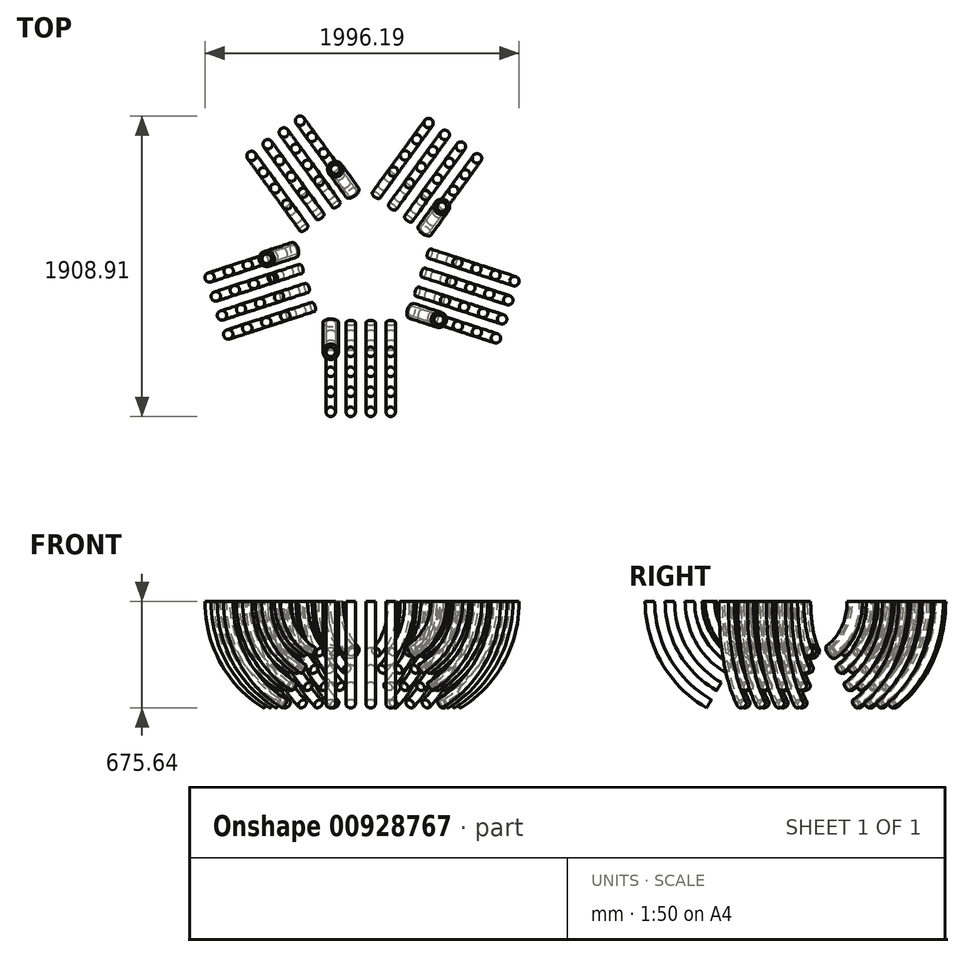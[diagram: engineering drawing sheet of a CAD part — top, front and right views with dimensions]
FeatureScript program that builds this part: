
annotation { "Feature Type Name" : "Feature", "Feature Type Description" : "" }
export const myFeature = defineFeature(function(context is Context, id is Id, definition is map)
    precondition{}
    {
        {
            var Q0;
            Q0=qCreatedBy(makeId("Top.planeOp"),FACE);
            var sketch = newSketch(context, id + "F0", { "sketchPlane" : qUnion([Q0])});
            skCircle(sketch, "E0", {"center": v(0, 0) * mm, "radius": 49.14 * mm});
            skArc(sketch, "E1", {"start": v(-10.74, 0) * mm, "mid": v(10.02, -3.86) * mm, "end": v(-7.96, 7.2) * mm});
            skLineSegment(sketch, "E2", {"start": v(-23.67, 49.14) * mm, "end": v(52.53, 49.14) * mm});
            skLineSegment(sketch, "E3", {"start": v(-23.28, 61.84) * mm, "end": v(52.92, 61.84) * mm});
            skLineSegment(sketch, "E4", {"start": v(-54.33, -21.78) * mm, "end": v(11.4, -68.22) * mm});
            skLineSegment(sketch, "E5", {"start": v(-72.68, -8.82) * mm, "end": v(-36.63, -34.28) * mm});
            skSolve(sketch);
        }
        {
            var Q0;
            Q0=qCreatedBy(makeId("Top.planeOp"),FACE);
            var sketch = newSketch(context, id + "F1", { "sketchPlane" : qUnion([Q0])});
            skPoint(sketch, "E6", {"position": v(-61.56, -16.56) * mm});
            skCircle(sketch, "E7.0", {"center": v(0, 0) * mm, "radius": 30.09 * mm});
            skCircle(sketch, "E8.0.1.0", {"center": v(0, -127) * mm, "radius": 30.09 * mm});
            skCircle(sketch, "E8.0.2.0", {"center": v(0, -254) * mm, "radius": 30.09 * mm});
            skCircle(sketch, "E8.0.3.0", {"center": v(0, -381) * mm, "radius": 30.09 * mm});
            skCircle(sketch, "E8.1.0.0", {"center": v(127, 0) * mm, "radius": 30.09 * mm});
            skCircle(sketch, "E8.1.1.0", {"center": v(127, -127) * mm, "radius": 30.09 * mm});
            skCircle(sketch, "E8.1.2.0", {"center": v(127, -254) * mm, "radius": 30.09 * mm});
            skCircle(sketch, "E8.1.3.0", {"center": v(127, -381) * mm, "radius": 30.09 * mm});
            skCircle(sketch, "E8.2.0.0", {"center": v(254, 0) * mm, "radius": 30.09 * mm});
            skCircle(sketch, "E8.2.1.0", {"center": v(254, -127) * mm, "radius": 30.09 * mm});
            skCircle(sketch, "E8.2.2.0", {"center": v(254, -254) * mm, "radius": 30.09 * mm});
            skCircle(sketch, "E8.2.3.0", {"center": v(254, -381) * mm, "radius": 30.09 * mm});
            skCircle(sketch, "E8.3.0.0", {"center": v(381, 0) * mm, "radius": 30.09 * mm});
            skCircle(sketch, "E8.3.1.0", {"center": v(381, -127) * mm, "radius": 30.09 * mm});
            skCircle(sketch, "E8.3.2.0", {"center": v(381, -254) * mm, "radius": 30.09 * mm});
            skCircle(sketch, "E8.3.3.0", {"center": v(381, -381) * mm, "radius": 30.09 * mm});
            skLineSegment(sketch, "E8.direction1", {"start": v(0, 0) * mm, "end": v(127, 0) * mm, "construction": true});
            skLineSegment(sketch, "E8.direction2", {"start": v(0, 0) * mm, "end": v(0, -127) * mm, "construction": true});
            skSolve(sketch);
        }
        {
            var Q0;
            Q0=qCreatedBy(makeId("Top.planeOp"),FACE);
            var sketch = newSketch(context, id + "F2", { "sketchPlane" : qUnion([Q0])});
            skLineSegment(sketch, "E9", {"start": v(-141.83, 369.08) * mm, "end": v(398.85, 369.08) * mm});
            skSolve(sketch);
        }
        {
            var Q0;
            Q0=makeQuery(id+"F1.imprint","IMPRINT",FACE,{"disambiguationData":[TD([[makeQuery(id+"F1.imprint","IMPRINT",EDGE,{"derivedFrom":sQuery(id+"F1.wireOp",EDGE,"E8.3.2.0")}),1.0]])]});
            var Q1;
            Q1=makeQuery(id+"F1.imprint","IMPRINT",FACE,{"disambiguationData":[TD([[makeQuery(id+"F1.imprint","IMPRINT",EDGE,{"derivedFrom":sQuery(id+"F1.wireOp",EDGE,"E8.3.0.0")}),1.0]])]});
            var Q2;
            Q2=makeQuery(id+"F1.imprint","IMPRINT",FACE,{"disambiguationData":[TD([[makeQuery(id+"F1.imprint","IMPRINT",EDGE,{"derivedFrom":sQuery(id+"F1.wireOp",EDGE,"E8.1.2.0")}),1.0]])]});
            var Q3;
            Q3=makeQuery(id+"F1.imprint","IMPRINT",FACE,{"disambiguationData":[TD([[makeQuery(id+"F1.imprint","IMPRINT",EDGE,{"derivedFrom":sQuery(id+"F1.wireOp",EDGE,"E8.3.1.0")}),1.0]])]});
            var Q4;
            Q4=makeQuery(id+"F1.imprint","IMPRINT",FACE,{"disambiguationData":[TD([[makeQuery(id+"F1.imprint","IMPRINT",EDGE,{"derivedFrom":sQuery(id+"F1.wireOp",EDGE,"E8.2.0.0")}),1.0]])]});
            var Q5;
            Q5=makeQuery(id+"F1.imprint","IMPRINT",FACE,{"disambiguationData":[TD([[makeQuery(id+"F1.imprint","IMPRINT",EDGE,{"derivedFrom":sQuery(id+"F1.wireOp",EDGE,"E8.2.1.0")}),1.0]])]});
            var Q6;
            Q6=makeQuery(id+"F1.imprint","IMPRINT",FACE,{"disambiguationData":[TD([[makeQuery(id+"F1.imprint","IMPRINT",EDGE,{"derivedFrom":sQuery(id+"F1.wireOp",EDGE,"E8.0.3.0")}),1.0]])]});
            var Q7;
            Q7=makeQuery(id+"F1.imprint","IMPRINT",FACE,{"disambiguationData":[TD([[makeQuery(id+"F1.imprint","IMPRINT",EDGE,{"derivedFrom":sQuery(id+"F1.wireOp",EDGE,"E8.1.3.0")}),1.0]])]});
            var Q8;
            Q8=makeQuery(id+"F1.imprint","IMPRINT",FACE,{"disambiguationData":[TD([[makeQuery(id+"F1.imprint","IMPRINT",EDGE,{"derivedFrom":sQuery(id+"F1.wireOp",EDGE,"E8.3.3.0")}),1.0]])]});
            var Q9;
            Q9=makeQuery(id+"F1.imprint","IMPRINT",FACE,{"disambiguationData":[TD([[makeQuery(id+"F1.imprint","IMPRINT",EDGE,{"derivedFrom":sQuery(id+"F1.wireOp",EDGE,"E8.2.2.0")}),1.0]])]});
            var Q10;
            Q10=makeQuery(id+"F1.imprint","IMPRINT",FACE,{"disambiguationData":[TD([[makeQuery(id+"F1.imprint","IMPRINT",EDGE,{"derivedFrom":sQuery(id+"F1.wireOp",EDGE,"E8.1.1.0")}),1.0]])]});
            var Q11;
            Q11=makeQuery(id+"F0.imprint","IMPRINT",FACE,{"disambiguationData":[TD([[makeQuery(id+"F0.imprint","IMPRINT",EDGE,{"derivedFrom":sQuery(id+"F0.wireOp",EDGE,"E0")}),1.0]])]});
            var Q12;
            Q12=makeQuery(id+"F1.imprint","IMPRINT",FACE,{"disambiguationData":[TD([[makeQuery(id+"F1.imprint","IMPRINT",EDGE,{"derivedFrom":sQuery(id+"F1.wireOp",EDGE,"E8.0.2.0")}),1.0]])]});
            var Q13;
            Q13=makeQuery(id+"F1.imprint","IMPRINT",FACE,{"disambiguationData":[TD([[makeQuery(id+"F1.imprint","IMPRINT",EDGE,{"derivedFrom":sQuery(id+"F1.wireOp",EDGE,"E8.1.0.0")}),1.0]])]});
            var Q14;
            Q14=makeQuery(id+"F1.imprint","IMPRINT",FACE,{"disambiguationData":[TD([[makeQuery(id+"F1.imprint","IMPRINT",EDGE,{"derivedFrom":sQuery(id+"F1.wireOp",EDGE,"E8.0.1.0")}),1.0]])]});
            var Q15;
            Q15=makeQuery(id+"F1.imprint","IMPRINT",FACE,{"disambiguationData":[TD([[makeQuery(id+"F1.imprint","IMPRINT",EDGE,{"derivedFrom":sQuery(id+"F1.wireOp",EDGE,"E8.2.3.0")}),1.0]])]});
            var Q16;
            Q16=makeQuery(id+"F1.imprint","IMPRINT",FACE,{"disambiguationData":[TD([[makeQuery(id+"F1.imprint","IMPRINT",EDGE,{"derivedFrom":sQuery(id+"F1.wireOp",EDGE,"E7.0")}),1.0]])]});
            var Q17;
            Q17=sQuery(id+"F2.wireOp",EDGE,"E9");
            revolve(context, id + "F3", {"surfaceOperationType" : NewSurfaceOperationType.NEW, "entities" : qUnion([Q0, Q1, Q2, Q3, Q4, Q5, Q6, Q7, Q8, Q9, Q10, Q11, Q12, Q13, Q14, Q15, Q16]), "axis" : qUnion([Q17]), "revolveType" : RevolveType.ONE_DIRECTION, "angle" : 60 * degree});
        }
        {
            var Q0;
            Q0=qCreatedBy(makeId("Right.planeOp"),FACE);
            cPlane(context, id + "F4", {"entities" : qUnion([Q0]), "cplaneType" : CPlaneType.OFFSET, "offset" : 203.2 * mm, "width" : 152.4 * mm, "height" : 152.4 * mm});
        }
        {
            var Q0;
            Q0=qCreatedBy(id+"F4.planeOp",FACE);
            var sketch = newSketch(context, id + "F5", { "sketchPlane" : qUnion([Q0])});
            skLineSegment(sketch, "E10", {"start": v(574.93, 283.66) * mm, "end": v(574.93, -226.8) * mm});
            skSolve(sketch);
        }
        {
            var Q0;
            Q0=makeQuery(id+"F3.opRevolve","SWEPT_BODY",BODY,{"disambiguationData":[OSD([sQuery(id+"F0.wireOp",EDGE,"E0")])]});
            var Q1;
            Q1=makeQuery(id+"F3.opRevolve","SWEPT_BODY",BODY,{"disambiguationData":[OSD([sQuery(id+"F1.wireOp",EDGE,"E7.0")])]});
            var Q2;
            Q2=makeQuery(id+"F3.opRevolve","SWEPT_BODY",BODY,{"disambiguationData":[OSD([sQuery(id+"F1.wireOp",EDGE,"E8.0.1.0")])]});
            var Q3;
            Q3=makeQuery(id+"F3.opRevolve","SWEPT_BODY",BODY,{"disambiguationData":[OSD([sQuery(id+"F1.wireOp",EDGE,"E8.0.2.0")])]});
            var Q4;
            Q4=makeQuery(id+"F3.opRevolve","SWEPT_BODY",BODY,{"disambiguationData":[OSD([sQuery(id+"F1.wireOp",EDGE,"E8.0.3.0")])]});
            var Q5;
            Q5=makeQuery(id+"F3.opRevolve","SWEPT_BODY",BODY,{"disambiguationData":[OSD([sQuery(id+"F1.wireOp",EDGE,"E8.1.0.0")])]});
            var Q6;
            Q6=makeQuery(id+"F3.opRevolve","SWEPT_BODY",BODY,{"disambiguationData":[OSD([sQuery(id+"F1.wireOp",EDGE,"E8.1.1.0")])]});
            var Q7;
            Q7=makeQuery(id+"F3.opRevolve","SWEPT_BODY",BODY,{"disambiguationData":[OSD([sQuery(id+"F1.wireOp",EDGE,"E8.1.2.0")])]});
            var Q8;
            Q8=makeQuery(id+"F3.opRevolve","SWEPT_BODY",BODY,{"disambiguationData":[OSD([sQuery(id+"F1.wireOp",EDGE,"E8.1.3.0")])]});
            var Q9;
            Q9=makeQuery(id+"F3.opRevolve","SWEPT_BODY",BODY,{"disambiguationData":[OSD([sQuery(id+"F1.wireOp",EDGE,"E8.2.0.0")])]});
            var Q10;
            Q10=makeQuery(id+"F3.opRevolve","SWEPT_BODY",BODY,{"disambiguationData":[OSD([sQuery(id+"F1.wireOp",EDGE,"E8.2.1.0")])]});
            var Q11;
            Q11=makeQuery(id+"F3.opRevolve","SWEPT_BODY",BODY,{"disambiguationData":[OSD([sQuery(id+"F1.wireOp",EDGE,"E8.2.2.0")])]});
            var Q12;
            Q12=makeQuery(id+"F3.opRevolve","SWEPT_BODY",BODY,{"disambiguationData":[OSD([sQuery(id+"F1.wireOp",EDGE,"E8.2.3.0")])]});
            var Q13;
            Q13=makeQuery(id+"F3.opRevolve","SWEPT_BODY",BODY,{"disambiguationData":[OSD([sQuery(id+"F1.wireOp",EDGE,"E8.3.0.0")])]});
            var Q14;
            Q14=makeQuery(id+"F3.opRevolve","SWEPT_BODY",BODY,{"disambiguationData":[OSD([sQuery(id+"F1.wireOp",EDGE,"E8.3.1.0")])]});
            var Q15;
            Q15=makeQuery(id+"F3.opRevolve","SWEPT_BODY",BODY,{"disambiguationData":[OSD([sQuery(id+"F1.wireOp",EDGE,"E8.3.2.0")])]});
            var Q16;
            Q16=makeQuery(id+"F3.opRevolve","SWEPT_BODY",BODY,{"disambiguationData":[OSD([sQuery(id+"F1.wireOp",EDGE,"E8.3.3.0")])]});
            var Q17;
            Q17=sQuery(id+"F5.wireOp",EDGE,"E10");
            circularPattern(context, id + "F6", {"entities" : qUnion([Q0, Q1, Q2, Q3, Q4, Q5, Q6, Q7, Q8, Q9, Q10, Q11, Q12, Q13, Q14, Q15, Q16]), "axis" : qUnion([Q17]), "angle" : 360 * degree, "instanceCount" : 5, "equalSpace" : true});
        }
    });
